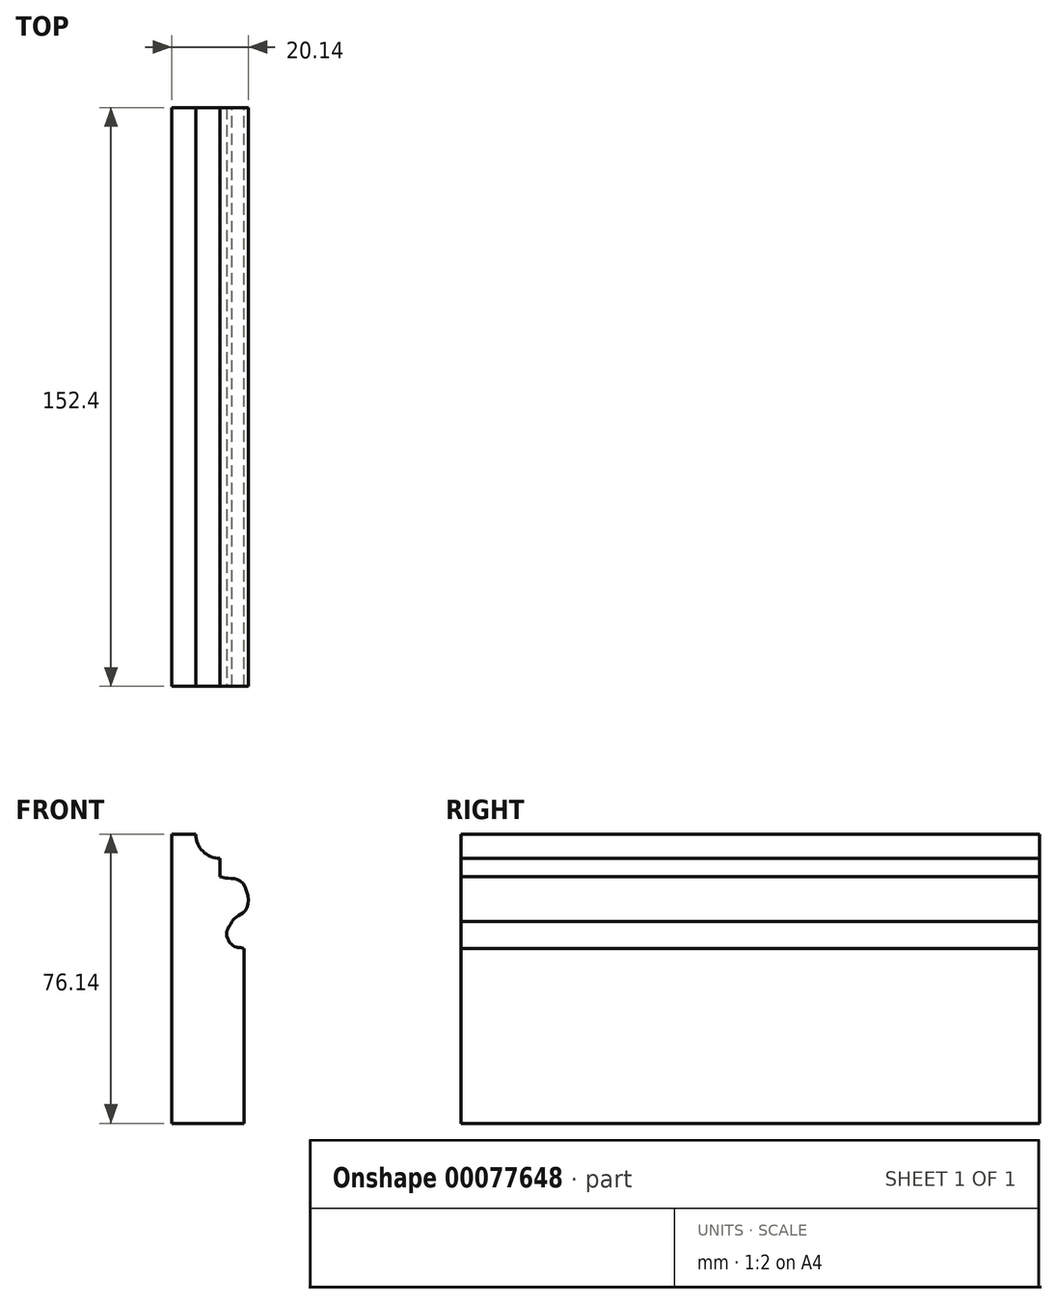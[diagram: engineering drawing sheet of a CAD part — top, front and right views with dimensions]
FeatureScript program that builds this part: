
annotation { "Feature Type Name" : "Feature", "Feature Type Description" : "" }
export const myFeature = defineFeature(function(context is Context, id is Id, definition is map)
    precondition{}
    {
        {
            var Q0;
            Q0=qCreatedBy(makeId("Front.planeOp"),FACE);
            var sketch = newSketch(context, id + "F0", { "sketchPlane" : qUnion([Q0])});
            skLineSegment(sketch, "E0", {"start": v(9.51, 7.93) * mm, "end": v(9.51, -38.07) * mm});
            skLineSegment(sketch, "E1", {"start": v(9.51, -38.07) * mm, "end": v(-9.52, -38.07) * mm});
            skLineSegment(sketch, "E2", {"start": v(-9.52, -38.07) * mm, "end": v(-9.52, 38.07) * mm});
            skLineSegment(sketch, "E3", {"start": v(-9.52, 38.07) * mm, "end": v(-3.18, 38.07) * mm});
            skLineSegment(sketch, "E4", {"start": v(3.17, 31.73) * mm, "end": v(3.17, 26.97) * mm});
            skArc(sketch, "E5", {"start": v(-3.18, 38.07) * mm, "mid": v(-1.32, 33.58) * mm, "end": v(3.17, 31.73) * mm});
            skFitSpline(sketch, "E6", {"points": [v(3.17, 26.97) * mm, v(4.97, 26.5) * mm, v(8.8, 25.53) * mm, v(10.34, 18.86) * mm, v(7.58, 16.29) * mm, v(6.34, 15.13) * mm]});
            skFitSpline(sketch, "E7", {"points": [v(6.34, 15.13) * mm, v(5.89, 14.18) * mm, v(4.92, 12.13) * mm, v(6.53, 8.78) * mm, v(8.6, 8.19) * mm, v(9.51, 7.93) * mm]});
            skSolve(sketch);
        }
        {
            var Q0;
            Q0=makeQuery(id+"F0.imprint","IMPRINT",FACE,{"disambiguationData":[TD([[makeQuery(id+"F0.imprint","IMPRINT",EDGE,{"derivedFrom":sQuery(id+"F0.wireOp",EDGE,"E0")}),-1.0]])]});
            extrude(context, id + "F1", {"entities" : qUnion([Q0]), "depth" : 152.4 * mm});
        }
    });
